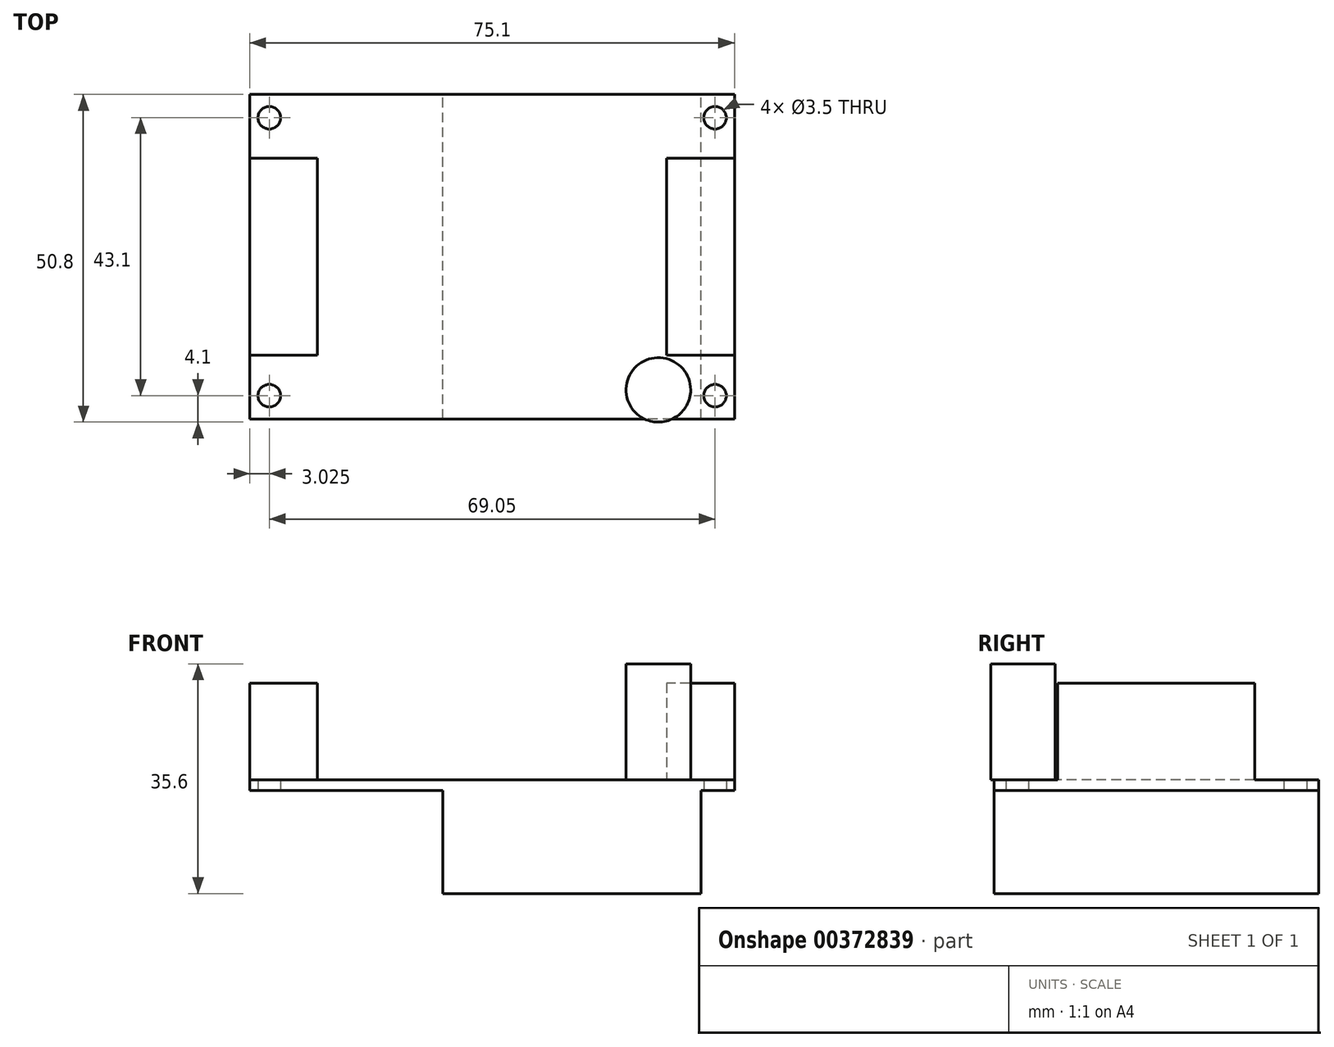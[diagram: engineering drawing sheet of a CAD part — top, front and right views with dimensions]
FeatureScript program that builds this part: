
annotation { "Feature Type Name" : "Feature", "Feature Type Description" : "" }
export const myFeature = defineFeature(function(context is Context, id is Id, definition is map)
    precondition{}
    {
        {
            var Q0;
            Q0=qCreatedBy(makeId("Top.planeOp"),FACE);
            var sketch = newSketch(context, id + "F0", { "sketchPlane" : qUnion([Q0])});
            skLineSegment(sketch, "E0.rect.bottom", {"start": v(37.55, -25.15) * mm, "end": v(-37.55, -25.15) * mm});
            skLineSegment(sketch, "E0.rect.top", {"start": v(37.55, 25.15) * mm, "end": v(-37.55, 25.15) * mm});
            skLineSegment(sketch, "E0.rect.left", {"start": v(37.55, -25.15) * mm, "end": v(37.55, 25.15) * mm});
            skLineSegment(sketch, "E0.rect.right", {"start": v(-37.55, -25.15) * mm, "end": v(-37.55, 25.15) * mm});
            skPoint(sketch, "E0.rect.middle", {"position": v(0, 0) * mm});
            skCircle(sketch, "E1", {"center": v(-34.53, 21.55) * mm, "radius": 1.75 * mm});
            skCircle(sketch, "E2", {"center": v(-34.53, -21.55) * mm, "radius": 1.75 * mm});
            skCircle(sketch, "E3", {"center": v(34.52, -21.55) * mm, "radius": 1.75 * mm});
            skCircle(sketch, "E4", {"center": v(34.52, 21.55) * mm, "radius": 1.75 * mm});
            skLineSegment(sketch, "E5", {"start": v(-34.52, 21.55) * mm, "end": v(-37.55, 0) * mm, "construction": true});
            skLineSegment(sketch, "E6", {"start": v(-37.55, 0) * mm, "end": v(-34.52, -21.55) * mm, "construction": true});
            skLineSegment(sketch, "E7", {"start": v(-34.53, 21.55) * mm, "end": v(0, 25.15) * mm, "construction": true});
            skLineSegment(sketch, "E8", {"start": v(0, 25.15) * mm, "end": v(34.52, 21.55) * mm, "construction": true});
            skSolve(sketch);
        }
        {
            var Q0;
            Q0=qSketchRegion(id+"F0",true);
            extrude(context, id + "F1", {"entities" : qUnion([Q0]), "depth" : 1.6 * mm});
        }
        {
            var Q0;
            Q0=makeQuery(id+"F1.opExtrude","CAP_FACE",FACE,{"disambiguationData":[OSD([sQuery(id+"F0.wireOp",EDGE,"E0.rect.bottom"),sQuery(id+"F0.wireOp",EDGE,"E0.rect.top"),sQuery(id+"F0.wireOp",EDGE,"E0.rect.left"),sQuery(id+"F0.wireOp",EDGE,"E0.rect.right"),sQuery(id+"F0.wireOp",EDGE,"E1"),sQuery(id+"F0.wireOp",EDGE,"E2"),sQuery(id+"F0.wireOp",EDGE,"E3"),sQuery(id+"F0.wireOp",EDGE,"E4")])],"isStart":false});
            var sketch = newSketch(context, id + "F2", { "sketchPlane" : qUnion([Q0])});
            skLineSegment(sketch, "E9.bottom", {"start": v(-37.55, 15.25) * mm, "end": v(-27.05, 15.25) * mm});
            skLineSegment(sketch, "E9.top", {"start": v(-37.55, -15.25) * mm, "end": v(-27.05, -15.25) * mm});
            skLineSegment(sketch, "E9.left", {"start": v(-37.55, 15.25) * mm, "end": v(-37.55, -15.25) * mm});
            skLineSegment(sketch, "E9.right", {"start": v(-27.05, 15.25) * mm, "end": v(-27.05, -15.25) * mm});
            skLineSegment(sketch, "E10.bottom", {"start": v(37.55, 15.25) * mm, "end": v(27.05, 15.25) * mm});
            skLineSegment(sketch, "E10.top", {"start": v(37.55, -15.25) * mm, "end": v(27.05, -15.25) * mm});
            skLineSegment(sketch, "E10.left", {"start": v(37.55, 15.25) * mm, "end": v(37.55, -15.25) * mm});
            skLineSegment(sketch, "E10.right", {"start": v(27.05, 15.25) * mm, "end": v(27.05, -15.25) * mm});
            skLineSegment(sketch, "E11", {"start": v(-27.05, 15.25) * mm, "end": v(-37.55, 25.15) * mm, "construction": true});
            skLineSegment(sketch, "E12", {"start": v(-27.05, -15.25) * mm, "end": v(-37.55, -25.15) * mm, "construction": true});
            skLineSegment(sketch, "E13", {"start": v(27.05, -15.25) * mm, "end": v(37.55, -25.15) * mm, "construction": true});
            skLineSegment(sketch, "E14", {"start": v(27.05, 15.25) * mm, "end": v(37.55, 25.15) * mm, "construction": true});
            skSolve(sketch);
        }
        {
            var Q0;
            Q0=qSketchRegion(id+"F2",true);
            extrude(context, id + "F3", {"entities" : qUnion([Q0]), "operationType" : NewBodyOperationType.ADD, "depth" : 15 * mm});
        }
        {
            var Q0;
            Q0=makeQuery(id+"F1.opExtrude","CAP_FACE",FACE,{"disambiguationData":[OSD([sQuery(id+"F0.wireOp",EDGE,"E0.rect.bottom"),sQuery(id+"F0.wireOp",EDGE,"E0.rect.top"),sQuery(id+"F0.wireOp",EDGE,"E0.rect.left"),sQuery(id+"F0.wireOp",EDGE,"E0.rect.right"),sQuery(id+"F0.wireOp",EDGE,"E1"),sQuery(id+"F0.wireOp",EDGE,"E2"),sQuery(id+"F0.wireOp",EDGE,"E3"),sQuery(id+"F0.wireOp",EDGE,"E4")])],"isStart":true});
            var sketch = newSketch(context, id + "F4", { "sketchPlane" : qUnion([Q0])});
            skLineSegment(sketch, "E15.bottom", {"start": v(-7.65, 25.15) * mm, "end": v(32.35, 25.15) * mm});
            skLineSegment(sketch, "E15.top", {"start": v(-7.65, -25.15) * mm, "end": v(32.35, -25.15) * mm});
            skLineSegment(sketch, "E15.left", {"start": v(-7.65, 25.15) * mm, "end": v(-7.65, -25.15) * mm});
            skLineSegment(sketch, "E15.right", {"start": v(32.35, 25.15) * mm, "end": v(32.35, -25.15) * mm});
            skSolve(sketch);
        }
        {
            var Q0;
            Q0=qSketchRegion(id+"F4",true);
            extrude(context, id + "F5", {"entities" : qUnion([Q0]), "operationType" : NewBodyOperationType.ADD, "depth" : 16 * mm});
        }
        {
            var Q0;
            Q0=makeQuery(id+"F1.opExtrude","CAP_FACE",FACE,{"disambiguationData":[OSD([sQuery(id+"F0.wireOp",EDGE,"E0.rect.bottom"),sQuery(id+"F0.wireOp",EDGE,"E0.rect.top"),sQuery(id+"F0.wireOp",EDGE,"E0.rect.left"),sQuery(id+"F0.wireOp",EDGE,"E0.rect.right"),sQuery(id+"F0.wireOp",EDGE,"E1"),sQuery(id+"F0.wireOp",EDGE,"E2"),sQuery(id+"F0.wireOp",EDGE,"E3"),sQuery(id+"F0.wireOp",EDGE,"E4")])],"isStart":false});
            var sketch = newSketch(context, id + "F6", { "sketchPlane" : qUnion([Q0])});
            skCircle(sketch, "E16", {"center": v(25.75, -20.65) * mm, "radius": 5 * mm});
            skSolve(sketch);
        }
        {
            var Q0;
            Q0=qSketchRegion(id+"F6",true);
            extrude(context, id + "F7", {"entities" : qUnion([Q0]), "operationType" : NewBodyOperationType.ADD, "depth" : 18 * mm});
        }
    });
